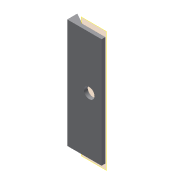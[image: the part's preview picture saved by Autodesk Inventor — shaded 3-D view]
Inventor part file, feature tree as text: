
AUTODESK INVENTOR PART (.ipt)
format: ipt  version: 2019 (Build 230136000, 136)  size: 91,648 bytes
history: native  units: mm
features: extrude x2, sketch x2, reference x2, other x2, plane x1, projected_geometry x1
ambient origin geometry x8: Origin, YZ Plane, XZ Plane, XY Plane, X Axis, Y Axis, Z Axis, Center Point
bodies: Solid1 (feature_tree)
feature tree (10):
  plane  "Work Plane1"
  extrude  "Extrusion1"  Depth=1.0mm TaperAngle=0.0deg
  extrude  "Extrusion2"  [1 undecoded]
  sketch  "Sketch1"  dims[d0=3.0mm d1=1.0mm d2=0.0mm]
  reference  "Reference1"
  reference  "Reference2"
  sketch  "Sketch2"  dims[d3=1.0mm d4=0.0mm]
  projected_geometry  "Projected Loop1"
  other  "cellSTORM_v5.iam"
  other  "cellSTORM_v5_chiptray_old_0:1"
note: 1 required parameter value undecoded (feature->parameter linkage not recoverable at this tier; creation-order binding heuristic only, values carry confidence <= 0.55)
